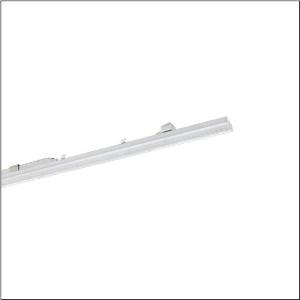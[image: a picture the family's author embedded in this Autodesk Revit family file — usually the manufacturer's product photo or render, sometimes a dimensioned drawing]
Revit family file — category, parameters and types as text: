
# Revit family: tl_l_5wd7a8h0g2b5
name_source: partatom
category: Lighting Fixtures
units: mm (PartAtom-declared; Revit-internal decimal feet)

## family parameters
Cut with Voids When Loaded = No
Host = Face
Light Source = No
Part Type = Normal
Room Calculation Point = No
Round Connector Dimension = Use Diameter
Shared = No

## types (1)
- --- (1 x LED, 850 lm, 4.5 W, 4000K)
    Apparent Load = 5 VA
    CIE Flux Codes = 49 84 98 100 100
    Color Rendering = 80
    Color Temperature = 4000K
    Default Elevation = 1800 mm
    Description = TL L, luminaire insert, of sheet steel, galvanised, coil coated, white, length: 1.500mm, width: 66mm, height: 67mm, surge protection,LED rated luminous flux: 4.990lm, light colour: 840, control gear: emergency light, with terminal, 3-pole, mains connection: 230..240V, AC, 50/60Hz, rated input power: 34W, primary optical cover: cover, of PMMA, light emission: direct distribution, protection rating (complete): as luminaire, insulation class (complete): insulation class I (protective earthing), certification: CE, impact resistance: IK06, permissible ambient temperature for indoor applications: +5..+35°C, packaging unit: 1 piece
    Height = 120 mm
    Lamp = 1 x LED
    Lamp Light Flux = 850 lm
    Lamp Power = 4.5 W
    Lamp count = 1
    Length = 1690 mm
    Luminous efficacy = 189 lm/W
    Manufacturer = Siteco
    ModVariant = No
    Model = 5WD7A8H0G2B5
    Mounting Place = Ceiling
    Mounting Type = Pendant
    Number of Poles = 1
    OnlyDefault = Yes
    Power Factor = 1
    Product Name = TL L
    Product group = luminaire insert
    ProductGroupID = 901
    Protection Class = Protection class I
    Protection Degree = Degree of protection
    RLX_Detail_Level = 1
    RLX_Emergency_Light_Flux = 0 lm
    RLX_Emergency_Type = 0
    RLX_Emergency_Type_DB = No
    RlxData = <blob elided: 17333 chars, md5=df8103d1>
    Socket = socket
    Standby Power = 0 W
    System Light Flux = 850 lm
    System Power = 5 W
    Type Comments = : emergency light operation: 3 h
    Type Image = l_1294382.jpg
    URL = http://relux.com
    VarID = @adj_030875
    Voltage = 0 V
    Weight = 0.00 kg
    Width = 208 mm

## geometry (parser evidence)
native form markers: Blend x4, Sweep x10
no freeform markers — native parametric forms only
